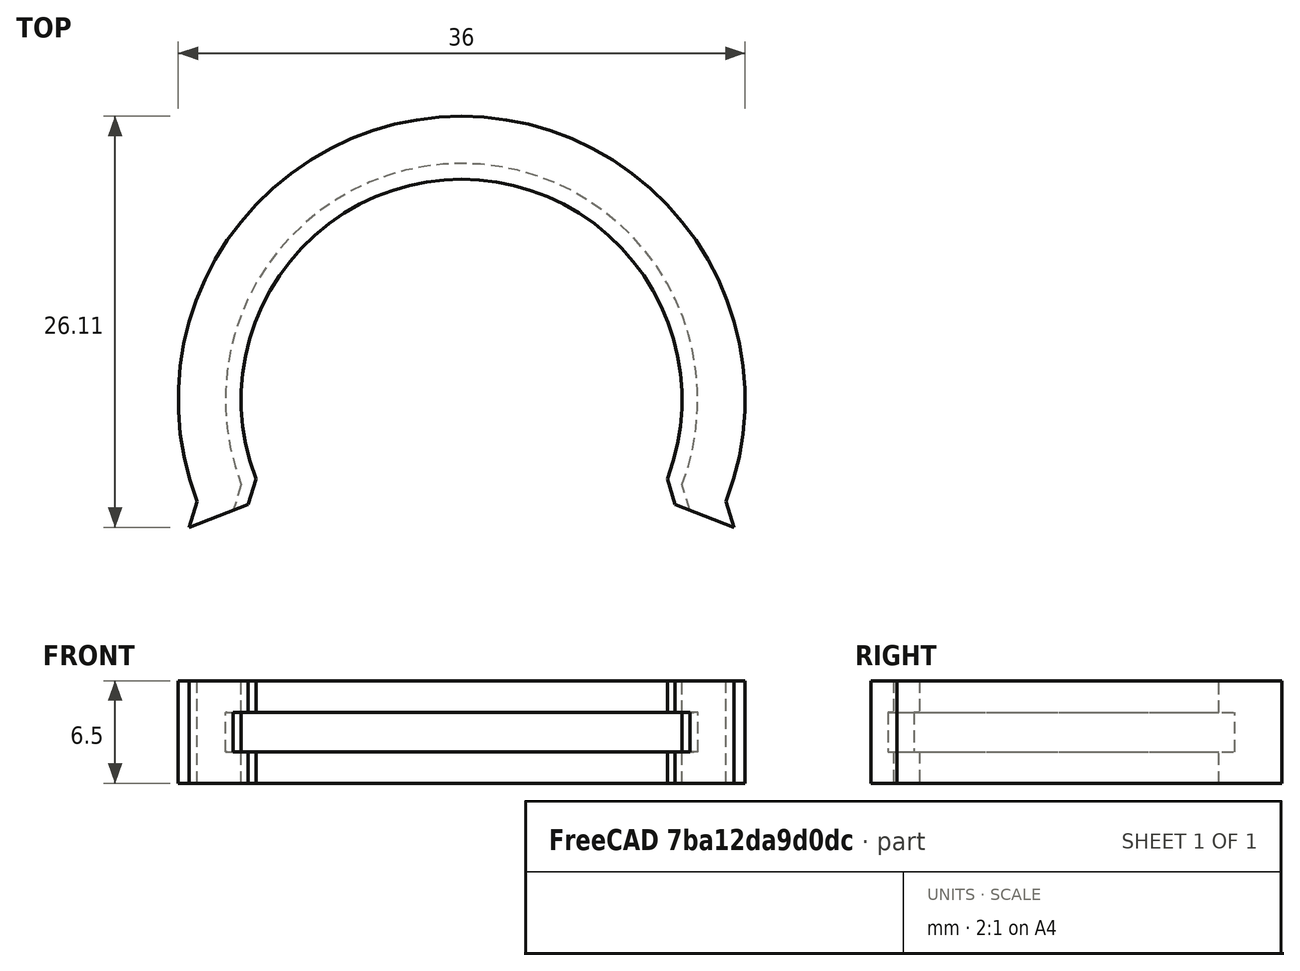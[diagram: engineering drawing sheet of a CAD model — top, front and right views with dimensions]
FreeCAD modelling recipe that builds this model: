
FCSTD DOCUMENT  (FreeCAD 0.19R20310 (Git))
Label: Clip
License: All rights reserved
LicenseURL: http://en.wikipedia.org/wiki/All_rights_reserved
objects: Sketcher::SketchObject×2, PartDesign::AdditivePipe×1, PartDesign::Body×1
note: 5 computed .brp shape members not serialized (recipe doc carries the construction recipe); baked Part::Feature solids carry a one-line shape summary decoded from their .brp

FEATURE [Sketcher::SketchObject] Sketch  label="Profil"
  MapMode = 5
  Placement = pos=(0,0,0) rot=(1,0,0;1.5708rad)
  Support = -> [XZ_Plane]
  sketch-geometry (8):
    g0: LineSegment StartX=14 StartY=0 StartZ=0 EndX=18 EndY=0 EndZ=0
    g1: LineSegment StartX=18 StartY=0 StartZ=0 EndX=18 EndY=6.5 EndZ=0
    g2: LineSegment StartX=18 StartY=6.5 StartZ=0 EndX=14 EndY=6.5 EndZ=0
    g3: LineSegment StartX=14 StartY=6.5 StartZ=0 EndX=14 EndY=4.5 EndZ=0
    g4: LineSegment StartX=14 StartY=4.5 StartZ=0 EndX=15 EndY=4.5 EndZ=0
    g5: LineSegment StartX=15 StartY=4.5 StartZ=0 EndX=15 EndY=2 EndZ=0
    g6: LineSegment StartX=15 StartY=2 StartZ=0 EndX=14 EndY=2 EndZ=0
    g7: LineSegment StartX=14 StartY=2 StartZ=0 EndX=14 EndY=0 EndZ=0
  constraints (24):
    c: PointOnObject(g0,g-1)
    c: Horizontal(g0)
    c: Coincident(g0,g1)
    c: Vertical(g1)
    c: Coincident(g1,g2)
    c: Horizontal(g2)
    c: Coincident(g2,g3)
    c: Vertical(g3)
    c: Coincident(g3,g4)
    c: Horizontal(g4)
    c: Coincident(g4,g5)
    c: Vertical(g5)
    c: Coincident(g5,g6)
    c: Horizontal(g6)
    c: Coincident(g6,g7)
    c: Coincident(g7,g0)
    c: Vertical(g7)
    c: DistanceX(g-1,g2) = 14
    c: Vertical(g3,g6)
    c: DistanceX(g-1,g5) = 15
    c: DistanceX(g-1,g0) = 18
    c: DistanceY(g3,g2) = 2
    c: DistanceY(g6,g3) = 2.5
    c: DistanceY(g0,g6) = 2
FEATURE [Sketcher::SketchObject] Sketch001  label="Path"
  MapMode = 5
  Support = -> [XY_Plane]
  sketch-geometry (3):
    g0: ArcOfCircle CenterX=0 CenterY=0 CenterZ=0 NormalX=0 NormalY=0 NormalZ=1 AngleXU=0 Radius=15 StartAngle=5.91598 EndAngle=9.79199
    g1: LineSegment StartX=14 StartY=-5.38516 StartZ=0 EndX=14.5 EndY=-7.02873 EndZ=0
    g2: LineSegment StartX=-14 StartY=-5.38516 StartZ=0 EndX=-14.5 EndY=-7.02873 EndZ=0
  constraints (8):
    c: Coincident(g0,g-1)
    c: Horizontal(g0,g0)
    c: Radius(g0) = 15
    c: Coincident(g1,g0)
    c: Symmetric(g1,g2,g-2)
    c: DistanceX(g2,g1) = 29
    c: Coincident(g0,g2)
    c: DistanceX(g0,g0) = 28
FEATURE [PartDesign::AdditivePipe] AdditivePipe
  AuxilleryCurvelinear = true
  AuxillerySpineTangent = false
  Binormal = (0,0,0)
  Mode = 0
  Placement = pos=(0,0,0) rot=(1,0,0;1.5708rad)
  Profile = -> Sketch
  Spine = -> Sketch001
  SpineTangent = false
  Transformation = 0
  Transition = 0
FEATURE [PartDesign::Body] Body
  Group = -> [Sketch,Sketch001,AdditivePipe]
  Origin = -> Origin
  Tip = -> AdditivePipe
